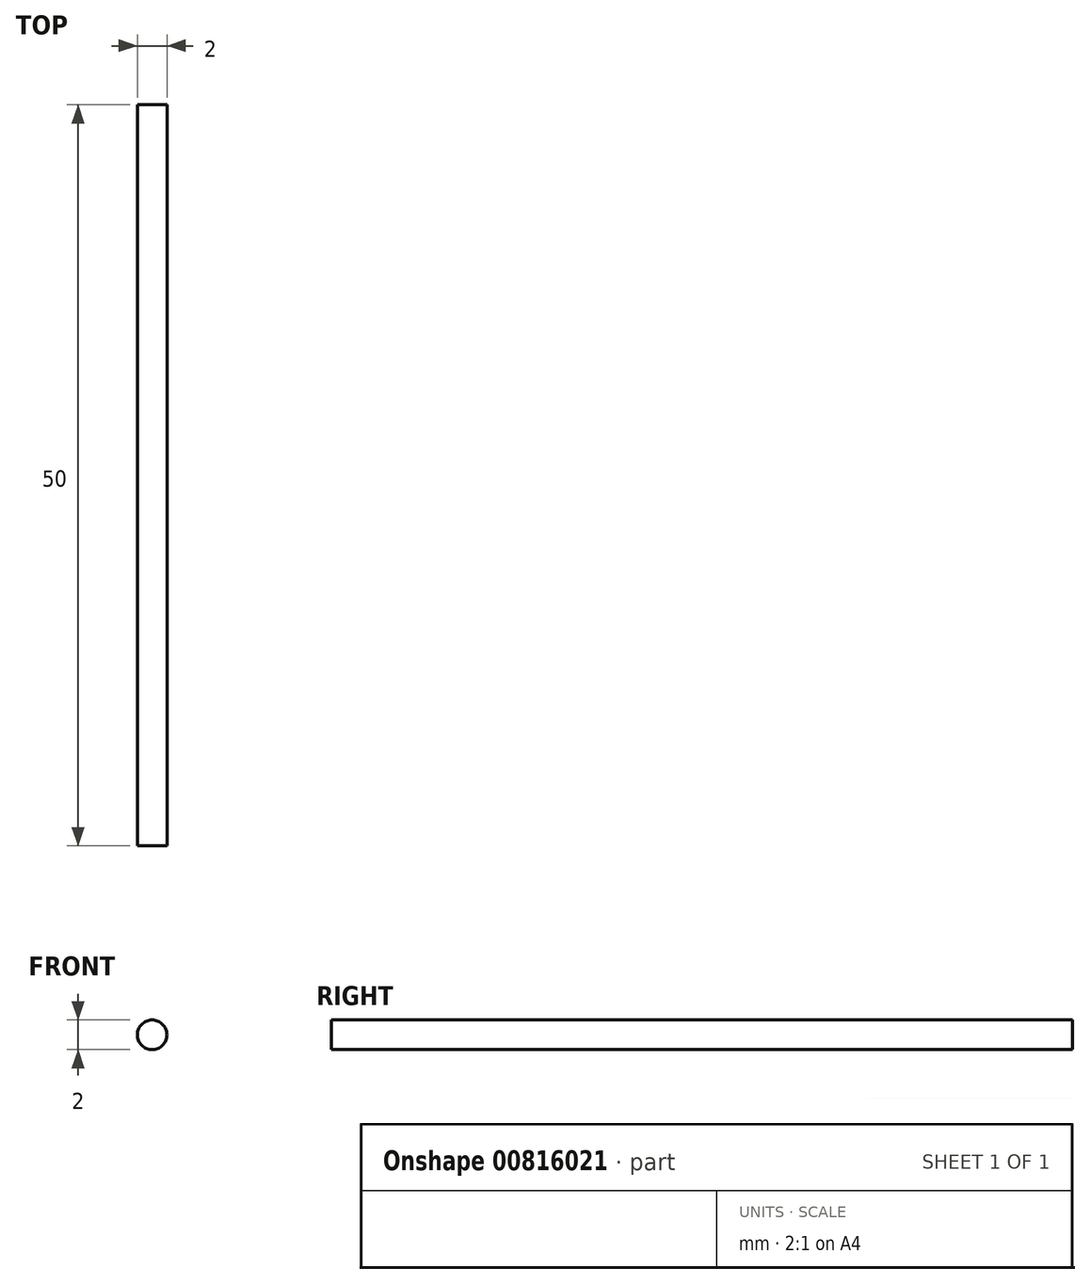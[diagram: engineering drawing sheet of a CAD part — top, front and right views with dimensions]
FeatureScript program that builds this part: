
annotation { "Feature Type Name" : "Feature", "Feature Type Description" : "" }
export const myFeature = defineFeature(function(context is Context, id is Id, definition is map)
    precondition{}
    {
        {
            var Q0;
            Q0=qCreatedBy(makeId("Front.planeOp"),FACE);
            var sketch = newSketch(context, id + "F0", { "sketchPlane" : qUnion([Q0])});
            skCircle(sketch, "E0", {"center": v(0, 0) * mm, "radius": 1 * mm});
            skSolve(sketch);
        }
        {
            var Q0;
            Q0=qSketchRegion(id+"F0",true);
            var Q1;
            Q1=makeQuery(id+"F0.imprint","IMPRINT",FACE,{"disambiguationData":[TD([[makeQuery(id+"F0.imprint","IMPRINT",EDGE,{"derivedFrom":sQuery(id+"F0.wireOp",EDGE,"E0")}),1.0]])]});
            extrude(context, id + "F1", {"entities" : qUnion([Q0, Q1]), "depth" : 50 * mm, "offsetDistance" : 25 * mm, "symmetric" : true});
        }
    });
